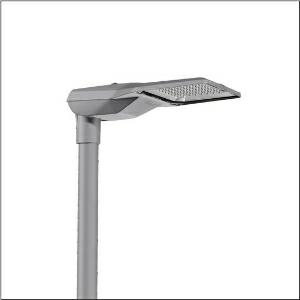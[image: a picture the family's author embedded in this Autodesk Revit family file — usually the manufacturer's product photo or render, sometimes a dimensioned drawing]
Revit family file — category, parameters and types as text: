
# Revit family: streetlight_sl_21_midi___p0_5a_5xe3v33s08mb_c878
name_source: partatom
category: Lighting Fixtures
units: mm (PartAtom-declared; Revit-internal decimal feet)

## family parameters
Cut with Voids When Loaded = No
Host = Face
Light Source = No
Part Type = Normal
Room Calculation Point = No
Round Connector Dimension = Use Diameter
Shared = No

## types (1)
- --- (1 x LED, 17960 lm, 136 W, 3000K)
    Apparent Load = 136 VA
    CIE Flux Codes = 37 73 96 100 100
    Color Rendering = 70
    Color Temperature = 3000K
    Default Elevation = 1800 mm
    Description = Streetlight SL 21 midi, mast luminaire, primary light control with lens, of PMMA, primary optical cover: cover, of toughened safety glass, transparent, light distribution: P0.5a, light emission: direct distribution, primary light characteristic: asymmetric, installation type: post-top, side-entry, LED, High Power LED, rated luminous flux: 17.960lm, luminous efficacy: 132lm/W, light colour: 730, colour temperature: 3000K, control gear: D4i, control: pre-setting: logarithmic dimming characteristic, flexible luminous flux parameterisation, time-dependent luminous flux control, constant luminous flux control, overheat protection, mains connection: 230..240V, AC, 50/60Hz, start of lifetime: 136W, end of service life: 142W, reduction: 61W, luminaire housing, of diecast aluminium, powder-coated, SITECO metallic grey (DB 702S), corrosivity category C5 high according to DIN EN ISO 12944, multi-level sealing system, sealing non-destructively replaceable, inclination adjustable: 0°, 5°, 10°, 15°, please order mast flange separately, length: 644mm, width: 335mm, height: 110mm, mast flange for spigot size: 42mm (side-entry): 5XC10008XM4, 60/48mm (side-entry/post-top): 5XC10108XM2, 76/60mm (side-entry/post-top): 5XC10108XM1, mounting height: 4..8m, Smart Interface above, protection rating (complete): IP66, insulation class (complete): insulation class II (safety insulation), certification: CE, ENEC, ENEC+, VDE, impact resistance: IK10, permissible operating ambient temperature for outdoor applications: -40..+50°C, standard-compliant lighting for roads and squares, packaging unit: 1 piece

Light Distribution: P0.5a
    Height = 111 mm
    Lamp = 1 x LED
    Lamp Light Flux = 17960 lm
    Lamp Power = 136 W
    Lamp count = 1
    Length = 644 mm
    Luminous efficacy = 132 lm/W
    Manufacturer = Siteco
    ModVariant = No
    Model = 5XE3V33S08MB
    Number of Poles = 1
    OnlyDefault = Yes
    Power Factor = 1
    Product Name = Streetlight SL 21 midi | P0.5a
    Product group = mast luminaire | pylon top
    ProductGroupID = 6100
    Protection Class = Protection class II
    Protection Degree = IP 66
    RLX_Detail_Level = 1
    RLX_Emergency_Light_Flux = 0 lm
    RLX_Emergency_Type = 0
    RLX_Emergency_Type_DB = No
    RlxData = <blob elided: 91201 chars, md5=bd0a5f42>
    Socket = socket
    Standby Power = 0 W
    System Light Flux = 17960 lm
    System Power = 136 W
    Type Comments = factory setting: luminous flux: 100 % | dim-lin: 254 | 695 mA
    Type Image = l_1004302.jpg
    URL = http://relux.com
    VarID = @adj_077655
    Voltage = 0 V
    Weight = 0.00 kg
    Width = 336 mm

## geometry (parser evidence)
native form markers: Blend x4, Sweep x12
no freeform markers — native parametric forms only
